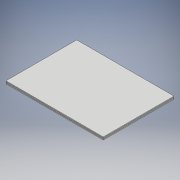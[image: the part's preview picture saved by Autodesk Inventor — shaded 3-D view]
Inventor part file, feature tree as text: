
AUTODESK INVENTOR PART (.ipt)
format: ipt  version: 2018 (Build 220112000, 112)  size: 100,864 bytes
history: native  units: mm
features: extrude x1, pattern_linear x1, sketch x1
ambient origin geometry x8: Origin, YZ Plane, XZ Plane, XY Plane, X Axis, Y Axis, Z Axis, Center Point
bodies: Solid1 (feature_tree)
feature tree (3):
  extrude  "Extrusion1"  Depth=160.0mm
  pattern_linear  "Rectangular Pattern1"  Spacing1=2.0mm  [1 undecoded]
  sketch  "Sketch1"  dims[d0=220.0mm d1=160.0mm d2=2.0mm d3=0.0mm d4=30.0mm d6=2.1mm]
note: 1 required parameter value undecoded (feature->parameter linkage not recoverable at this tier; creation-order binding heuristic only, values carry confidence <= 0.55)
